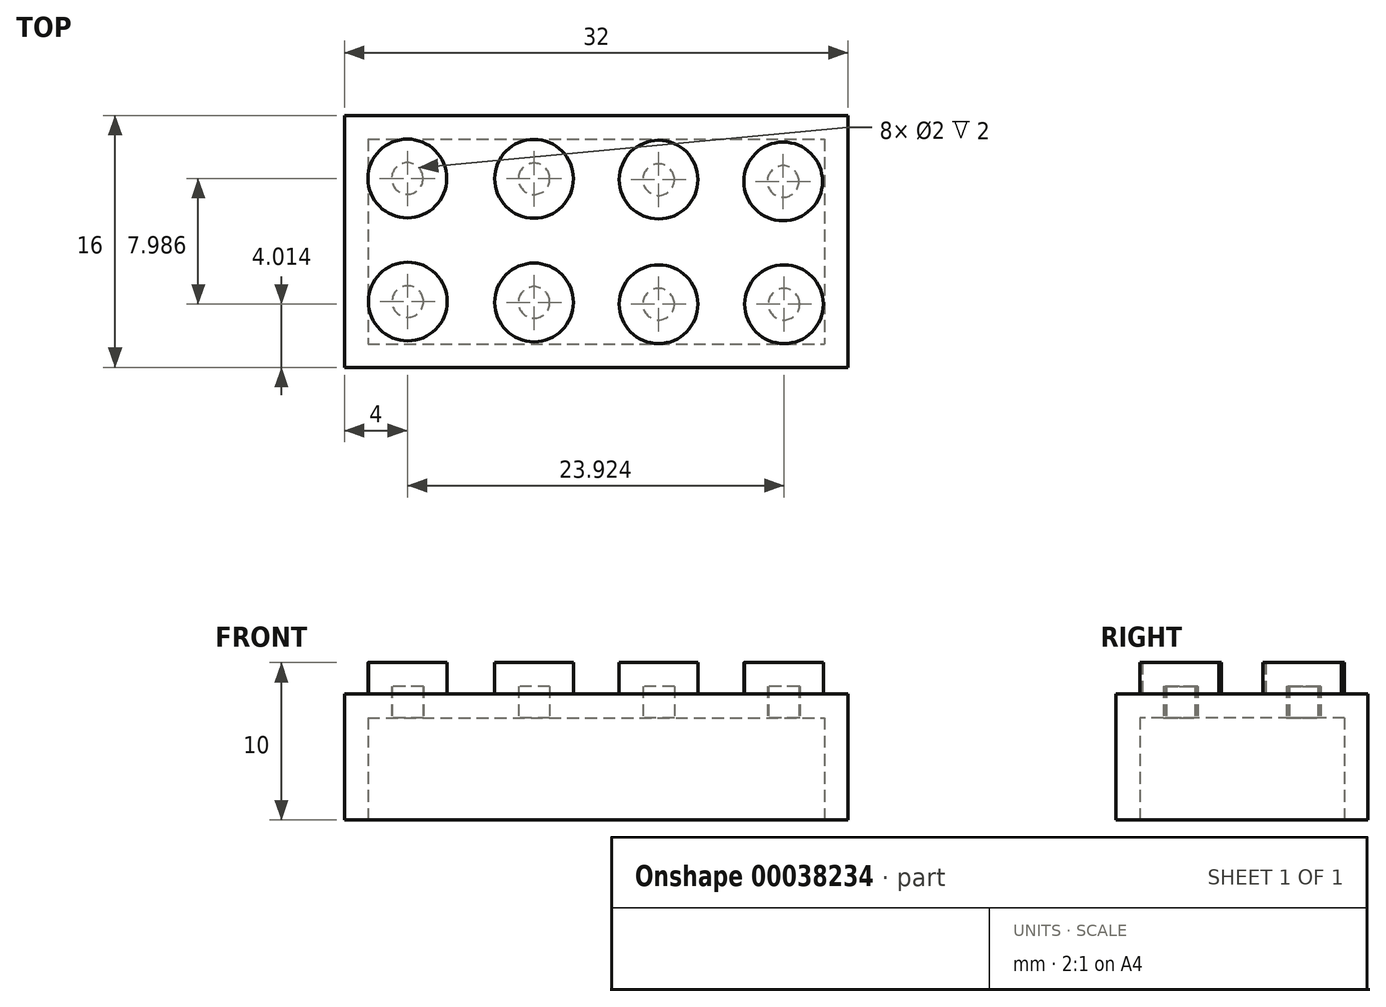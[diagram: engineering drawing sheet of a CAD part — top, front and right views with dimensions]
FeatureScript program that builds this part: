
annotation { "Feature Type Name" : "Feature", "Feature Type Description" : "" }
export const myFeature = defineFeature(function(context is Context, id is Id, definition is map)
    precondition{}
    {
        {
            var Q0;
            Q0=qCreatedBy(makeId("Top.planeOp"),FACE);
            var sketch = newSketch(context, id + "F0", { "sketchPlane" : qUnion([Q0])});
            skLineSegment(sketch, "E0.rect.bottom", {"start": v(-16, 8) * mm, "end": v(16, 8) * mm});
            skLineSegment(sketch, "E0.rect.top", {"start": v(-16, -8) * mm, "end": v(16, -8) * mm});
            skLineSegment(sketch, "E0.rect.left", {"start": v(-16, 8) * mm, "end": v(-16, -8) * mm});
            skLineSegment(sketch, "E0.rect.right", {"start": v(16, 8) * mm, "end": v(16, -8) * mm});
            skPoint(sketch, "E0.rect.middle", {"position": v(0, 0) * mm});
            skSolve(sketch);
        }
        {
            var Q0;
            Q0 = qSketchRegion(id + "F0", true);
            extrude(context, id + "F1", {"entities" : qUnion([Q0]), "depth" : 8 * mm});
        }
        {
            var Q0;
            Q0=makeQuery(id+"F1.opExtrude","CAP_FACE",FACE,{"disambiguationData":[OSD([sQuery(id+"F0.wireOp",EDGE,"E0.rect.bottom"),sQuery(id+"F0.wireOp",EDGE,"E0.rect.top"),sQuery(id+"F0.wireOp",EDGE,"E0.rect.left"),sQuery(id+"F0.wireOp",EDGE,"E0.rect.right")])],"isStart":false});
            var sketch = newSketch(context, id + "F2", { "sketchPlane" : qUnion([Q0])});
            skLineSegment(sketch, "E1", {"start": v(-16, 10.83) * mm, "end": v(16, 10.83) * mm, "construction": true});
            skLineSegment(sketch, "E2", {"start": v(16, 10.83) * mm, "end": v(16, 8) * mm, "construction": true});
            skLineSegment(sketch, "E3", {"start": v(-16, 10.83) * mm, "end": v(-16, 8) * mm, "construction": true});
            skLineSegment(sketch, "E4", {"start": v(-16, 8) * mm, "end": v(-12, 8) * mm, "construction": true});
            skLineSegment(sketch, "E5", {"start": v(-12, 8) * mm, "end": v(-4, 8) * mm, "construction": true});
            skLineSegment(sketch, "E6", {"start": v(-4, 8) * mm, "end": v(4, 8) * mm, "construction": true});
            skLineSegment(sketch, "E7", {"start": v(4, 8) * mm, "end": v(12, 8) * mm, "construction": true});
            skLineSegment(sketch, "E8", {"start": v(12, 8) * mm, "end": v(16, 8) * mm, "construction": true});
            skLineSegment(sketch, "E9", {"start": v(-12, 8) * mm, "end": v(-12, -8) * mm, "construction": true});
            skLineSegment(sketch, "E10", {"start": v(-4, 8) * mm, "end": v(-4, -8) * mm, "construction": true});
            skLineSegment(sketch, "E11", {"start": v(4, 8) * mm, "end": v(4, -8) * mm, "construction": true});
            skLineSegment(sketch, "E12", {"start": v(12, 8) * mm, "end": v(12, -8) * mm, "construction": true});
            skLineSegment(sketch, "E13", {"start": v(-16, 8) * mm, "end": v(-16, 4) * mm, "construction": true});
            skLineSegment(sketch, "E14", {"start": v(-16, 4) * mm, "end": v(-16, 0) * mm, "construction": true});
            skLineSegment(sketch, "E15", {"start": v(-16, 0) * mm, "end": v(-16, -4) * mm, "construction": true});
            skLineSegment(sketch, "E16", {"start": v(-16, -4) * mm, "end": v(-16, -8) * mm, "construction": true});
            skLineSegment(sketch, "E17", {"start": v(-16, 4) * mm, "end": v(16, 4) * mm, "construction": true});
            skLineSegment(sketch, "E18", {"start": v(-16, 0) * mm, "end": v(16, 0) * mm, "construction": true});
            skLineSegment(sketch, "E19", {"start": v(-16, -4) * mm, "end": v(16, -4) * mm, "construction": true});
            skCircle(sketch, "E20", {"center": v(-12, 4) * mm, "radius": 2.5 * mm});
            skCircle(sketch, "E21", {"center": v(-3.95, 3.98) * mm, "radius": 2.5 * mm});
            skCircle(sketch, "E22", {"center": v(3.96, 3.92) * mm, "radius": 2.5 * mm});
            skCircle(sketch, "E23", {"center": v(11.87, 3.81) * mm, "radius": 2.5 * mm});
            skCircle(sketch, "E24", {"center": v(-11.97, -3.82) * mm, "radius": 2.5 * mm});
            skCircle(sketch, "E25", {"center": v(-3.95, -3.87) * mm, "radius": 2.5 * mm});
            skCircle(sketch, "E26", {"center": v(3.96, -3.99) * mm, "radius": 2.5 * mm});
            skCircle(sketch, "E27", {"center": v(11.92, -3.99) * mm, "radius": 2.5 * mm});
            skSolve(sketch);
        }
        {
            var Q0;
            Q0 = qSketchRegion(id + "F2", true);
            extrude(context, id + "F3", {"entities" : qUnion([Q0]), "operationType" : NewBodyOperationType.ADD, "depth" : 2 * mm});
        }
        {
            var Q0;
            Q0=makeQuery(id+"F1.opExtrude","CAP_FACE",FACE,{"disambiguationData":[OSD([sQuery(id+"F0.wireOp",EDGE,"E0.rect.bottom"),sQuery(id+"F0.wireOp",EDGE,"E0.rect.top"),sQuery(id+"F0.wireOp",EDGE,"E0.rect.left"),sQuery(id+"F0.wireOp",EDGE,"E0.rect.right")])],"isStart":true});
            shell(context, id + "F4", {"entities" : qUnion([Q0]), "thickness" : 1.5 * mm});
        }
    });
